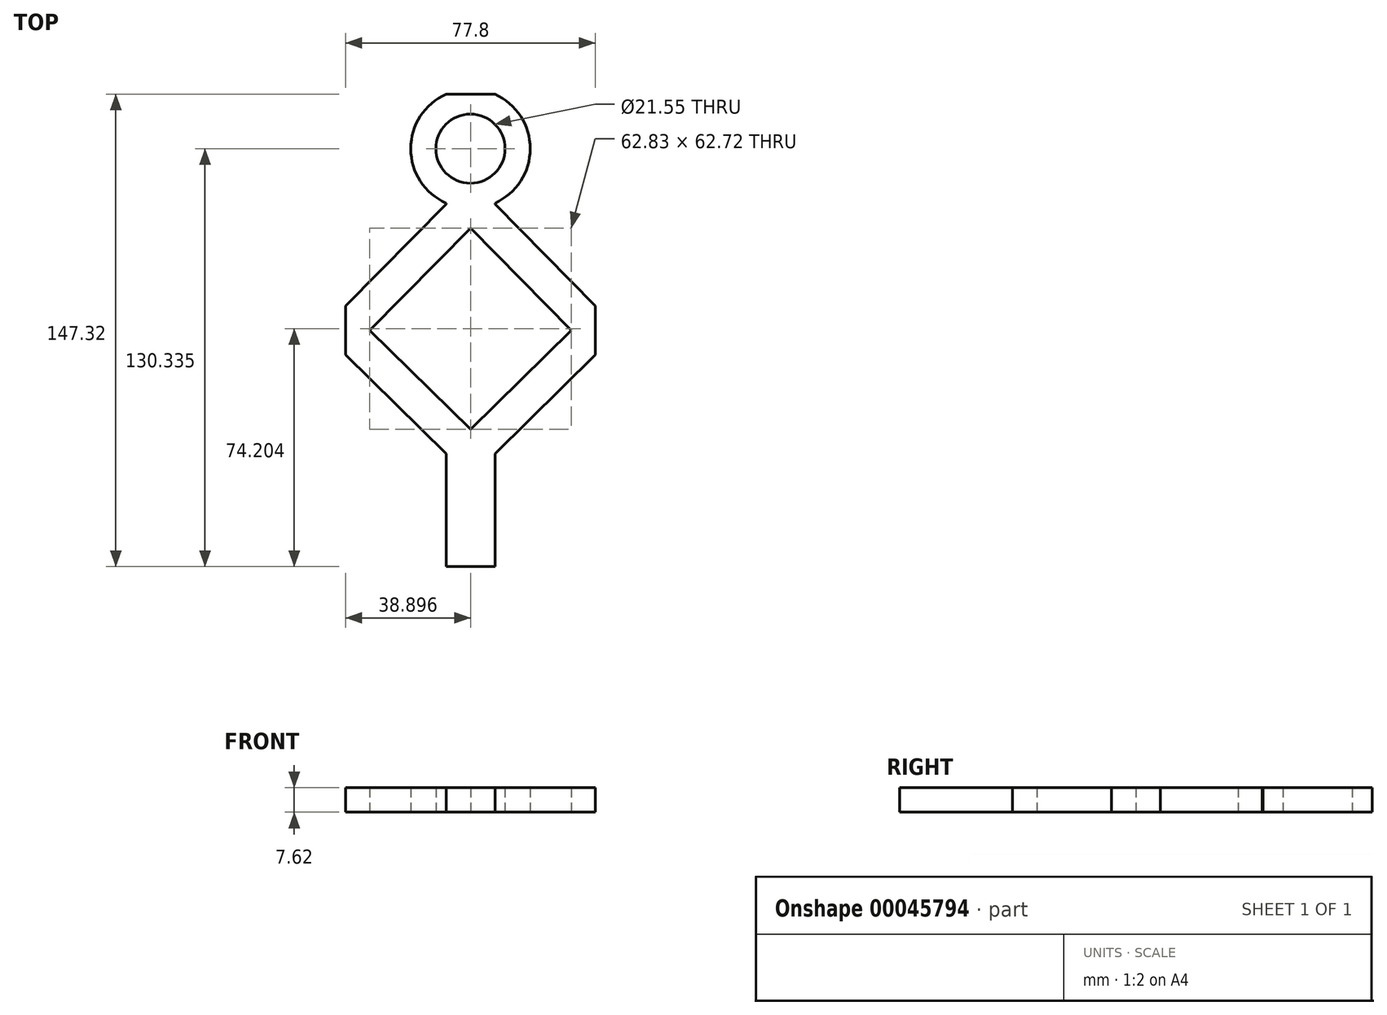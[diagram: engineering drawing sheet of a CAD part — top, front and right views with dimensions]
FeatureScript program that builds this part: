
annotation { "Feature Type Name" : "Feature", "Feature Type Description" : "" }
export const myFeature = defineFeature(function(context is Context, id is Id, definition is map)
    precondition{}
    {
        {
            var Q0;
            Q0=qCreatedBy(makeId("Top.planeOp"),FACE);
            var sketch = newSketch(context, id + "F0", { "sketchPlane" : qUnion([Q0])});
            skCircle(sketch, "E0", {"center": v(0, 0) * mm, "radius": 3.18 * mm, "construction": true});
            skLineSegment(sketch, "E1", {"start": v(0, 0) * mm, "end": v(0, 6.7) * mm, "construction": true});
            skLineSegment(sketch, "E2", {"start": v(0, 0) * mm, "end": v(9.9, 0) * mm, "construction": true});
            skLineSegment(sketch, "E3", {"start": v(0, 6.7) * mm, "end": v(9.9, 6.7) * mm, "construction": true});
            skLineSegment(sketch, "E4", {"start": v(9.9, 6.7) * mm, "end": v(9.9, 0) * mm, "construction": true});
            skLineSegment(sketch, "E5", {"start": v(9.9, 6.7) * mm, "end": v(9.9, -140.61) * mm, "construction": true});
            skLineSegment(sketch, "E6", {"start": v(9.9, -140.61) * mm, "end": v(-67.9, -140.61) * mm, "construction": true});
            skLineSegment(sketch, "E7", {"start": v(-67.9, -140.61) * mm, "end": v(-67.9, 6.7) * mm, "construction": true});
            skLineSegment(sketch, "E8", {"start": v(-67.9, 6.7) * mm, "end": v(0, 6.7) * mm, "construction": true});
            skLineSegment(sketch, "E9", {"start": v(-67.9, 6.7) * mm, "end": v(-29, 6.7) * mm, "construction": true});
            skLineSegment(sketch, "E10", {"start": v(-29, 6.7) * mm, "end": v(-29, -140.61) * mm, "construction": true});
            skLineSegment(sketch, "E11", {"start": v(9.9, -66.95) * mm, "end": v(-29, -27.44) * mm, "construction": true});
            skLineSegment(sketch, "E12", {"start": v(-29, -27.44) * mm, "end": v(-67.9, -66.95) * mm, "construction": true});
            skLineSegment(sketch, "E13", {"start": v(-67.9, -66.95) * mm, "end": v(-29, -105.25) * mm, "construction": true});
            skLineSegment(sketch, "E14", {"start": v(-29, -105.25) * mm, "end": v(9.9, -66.95) * mm, "construction": true});
            skLineSegment(sketch, "E15", {"start": v(-36.61, -140.61) * mm, "end": v(-36.61, -105.37) * mm});
            skPoint(sketch, "E16.endSnap0", {"position": v(-36.61, -119.18) * mm});
            skLineSegment(sketch, "E17", {"start": v(-29, -27.44) * mm, "end": v(-29, -19.82) * mm, "construction": true});
            skLineSegment(sketch, "E18", {"start": v(-29, -105.25) * mm, "end": v(-29, -112.87) * mm, "construction": true});
            skLineSegment(sketch, "E19", {"start": v(-67.9, -59.33) * mm, "end": v(-36.61, -27.56) * mm});
            skLineSegment(sketch, "E20", {"start": v(-21.37, -140.61) * mm, "end": v(-21.37, -105.37) * mm});
            skLineSegment(sketch, "E21", {"start": v(-21.37, -27.56) * mm, "end": v(9.9, -59.33) * mm});
            skLineSegment(sketch, "E22", {"start": v(-67.9, -74.57) * mm, "end": v(-36.61, -105.37) * mm});
            skLineSegment(sketch, "E23", {"start": v(9.9, -74.57) * mm, "end": v(-21.37, -105.37) * mm});
            skLineSegment(sketch, "E24", {"start": v(-21.37, 6.7) * mm, "end": v(-21.37, -17.9) * mm});
            skPoint(sketch, "E25.orphan", {"position": v(-36.61, -97.75) * mm});
            skLineSegment(sketch, "E26", {"start": v(-67.9, -66.95) * mm, "end": v(9.9, -66.95) * mm, "construction": true});
            skLineSegment(sketch, "E27", {"start": v(-67.9, -66.95) * mm, "end": v(-60.4, -66.95) * mm, "construction": true});
            skLineSegment(sketch, "E28", {"start": v(-29, -27.44) * mm, "end": v(-29, -35.05) * mm, "construction": true});
            skLineSegment(sketch, "E29", {"start": v(9.9, -66.95) * mm, "end": v(2.42, -66.95) * mm, "construction": true});
            skLineSegment(sketch, "E30", {"start": v(-29, -105.25) * mm, "end": v(-29, -97.77) * mm, "construction": true});
            skLineSegment(sketch, "E31", {"start": v(-60.4, -66.95) * mm, "end": v(-29, -97.77) * mm});
            skLineSegment(sketch, "E32", {"start": v(-29, -97.77) * mm, "end": v(2.42, -66.95) * mm});
            skLineSegment(sketch, "E33", {"start": v(2.42, -66.95) * mm, "end": v(-29, -35.05) * mm});
            skLineSegment(sketch, "E34", {"start": v(-29, -35.05) * mm, "end": v(-60.4, -66.95) * mm});
            skLineSegment(sketch, "E35", {"start": v(-67.9, -59.33) * mm, "end": v(-67.9, -74.57) * mm});
            skLineSegment(sketch, "E36", {"start": v(-36.61, 6.7) * mm, "end": v(-21.37, 6.7) * mm});
            skLineSegment(sketch, "E37", {"start": v(9.9, -74.57) * mm, "end": v(9.9, -59.33) * mm});
            skLineSegment(sketch, "E38", {"start": v(-21.37, -140.61) * mm, "end": v(-36.61, -140.61) * mm});
            skLineSegment(sketch, "E39", {"start": v(-21.37, 6.7) * mm, "end": v(-21.37, -2.65) * mm, "construction": true});
            skLineSegment(sketch, "E40", {"start": v(-21.37, -2.65) * mm, "end": v(-21.37, -17.9) * mm, "construction": true});
            skCircle(sketch, "E41", {"center": v(-29, -10.27) * mm, "radius": 10.78 * mm});
            skLineSegment(sketch, "E42.trimOffspring", {"start": v(-36.61, -27.26) * mm, "end": v(-36.61, -27.56) * mm});
            skLineSegment(sketch, "E43.trimOffspring", {"start": v(-21.37, -27.26) * mm, "end": v(-21.37, -27.56) * mm});
            skPoint(sketch, "E44.start.orphan", {"position": v(-29, -2.65) * mm});
            skPoint(sketch, "E45.orphan", {"position": v(-36.61, -2.65) * mm});
            skArc(sketch, "E46", {"start": v(-36.61, 6.7) * mm, "mid": v(-47.6, -10.27) * mm, "end": v(-36.61, -27.26) * mm});
            skArc(sketch, "E47.trimOffspring", {"start": v(-21.37, -27.26) * mm, "mid": v(-10.38, -10.27) * mm, "end": v(-21.37, 6.7) * mm});
            skSolve(sketch);
        }
        {
            var Q0;
            Q0 = qSketchRegion(id + "F0", true);
            extrude(context, id + "F1", {"entities" : qUnion([Q0]), "depth" : 7.62 * mm});
        }
    });
